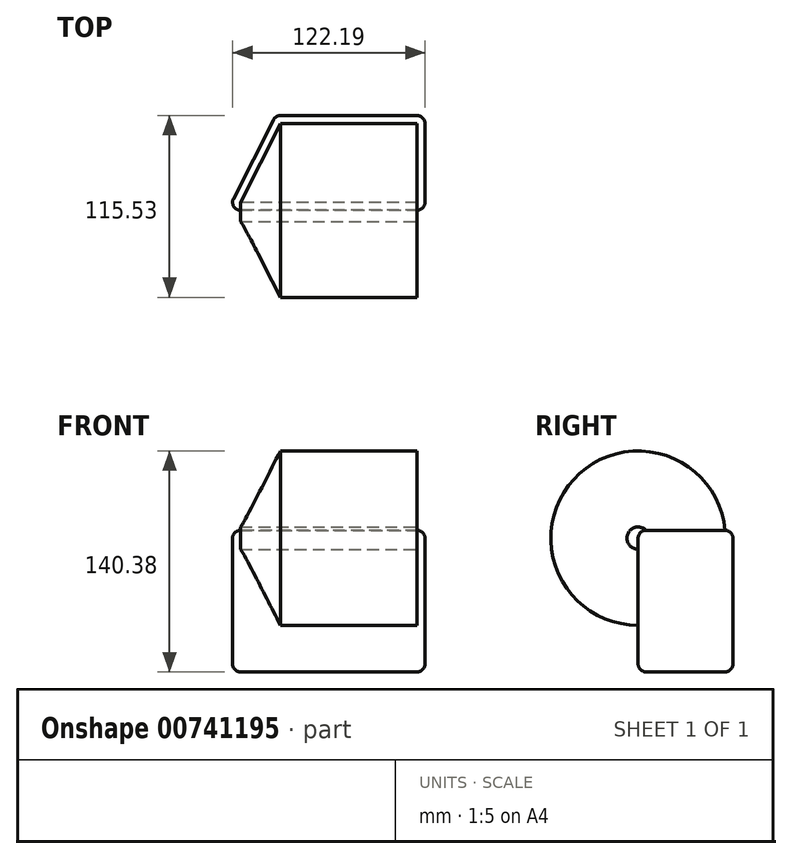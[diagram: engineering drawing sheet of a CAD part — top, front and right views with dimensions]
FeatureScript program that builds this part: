
annotation { "Feature Type Name" : "Feature", "Feature Type Description" : "" }
export const myFeature = defineFeature(function(context is Context, id is Id, definition is map)
    precondition{}
    {
        {
            var Q0;
            Q0=qCreatedBy(makeId("Top.planeOp"),FACE);
            var sketch = newSketch(context, id + "F0", { "sketchPlane" : qUnion([Q0])});
            skLineSegment(sketch, "E0", {"start": v(0, 0) * mm, "end": v(-125.32, 0) * mm});
            skLineSegment(sketch, "E1", {"start": v(-125.32, 0) * mm, "end": v(-94.92, 60.15) * mm});
            skLineSegment(sketch, "E2", {"start": v(-94.92, 60.15) * mm, "end": v(0, 60.15) * mm});
            skLineSegment(sketch, "E3", {"start": v(0, 60.15) * mm, "end": v(0, 0) * mm});
            skSolve(sketch);
        }
        {
            var Q0;
            Q0=makeQuery(id+"F0.imprint","IMPRINT",FACE,{"disambiguationData":[TD([[makeQuery(id+"F0.imprint","IMPRINT",EDGE,{"derivedFrom":sQuery(id+"F0.wireOp",EDGE,"E0")}),-1.0]])]});
            extrude(context, id + "F1", {"entities" : qUnion([Q0]), "depth" : 90 * mm, "offsetDistance" : 25 * mm});
        }
        {
            var Q0;
            Q0=makeQuery(id+"F1.opExtrude","CAP_EDGE",EDGE,{"disambiguationData":[OSD([sQuery(id+"F0.wireOp",EDGE,"E2")])],"isStart":false});
            var Q1;
            Q1=makeQuery(id+"F1.opExtrude","CAP_EDGE",EDGE,{"disambiguationData":[OSD([sQuery(id+"F0.wireOp",EDGE,"E3")])],"isStart":false});
            var Q2;
            Q2=makeQuery(id+"F1.opExtrude","CAP_EDGE",EDGE,{"disambiguationData":[OSD([sQuery(id+"F0.wireOp",EDGE,"E0")])],"isStart":false});
            var Q3;
            Q3=makeQuery(id+"F1.opExtrude","CAP_EDGE",EDGE,{"disambiguationData":[OSD([sQuery(id+"F0.wireOp",EDGE,"E1")])],"isStart":false});
            var Q4;
            Q4=makeQuery(id+"F1.opExtrude","SWEPT_EDGE",EDGE,{"disambiguationData":[OSD([sQuery(id+"F0.wireOp",EDGE,"E2"),sQuery(id+"F0.wireOp",EDGE,"E3")])]});
            var Q5;
            Q5=makeQuery(id+"F1.opExtrude","SWEPT_EDGE",EDGE,{"disambiguationData":[OSD([sQuery(id+"F0.wireOp",EDGE,"E0"),sQuery(id+"F0.wireOp",EDGE,"E3")])]});
            var Q6;
            Q6=makeQuery(id+"F1.opExtrude","SWEPT_EDGE",EDGE,{"disambiguationData":[OSD([sQuery(id+"F0.wireOp",EDGE,"E1"),sQuery(id+"F0.wireOp",EDGE,"E2")])]});
            var Q7;
            Q7=makeQuery(id+"F1.opExtrude","SWEPT_EDGE",EDGE,{"disambiguationData":[OSD([sQuery(id+"F0.wireOp",EDGE,"E0"),sQuery(id+"F0.wireOp",EDGE,"E1")])]});
            var Q8;
            Q8=makeQuery(id+"F1.opExtrude","CAP_EDGE",EDGE,{"disambiguationData":[OSD([sQuery(id+"F0.wireOp",EDGE,"E1")])],"isStart":true});
            var Q9;
            Q9=makeQuery(id+"F1.opExtrude","CAP_EDGE",EDGE,{"disambiguationData":[OSD([sQuery(id+"F0.wireOp",EDGE,"E0")])],"isStart":true});
            var Q10;
            Q10=makeQuery(id+"F1.opExtrude","CAP_EDGE",EDGE,{"disambiguationData":[OSD([sQuery(id+"F0.wireOp",EDGE,"E2")])],"isStart":true});
            var Q11;
            Q11=makeQuery(id+"F1.opExtrude","CAP_EDGE",EDGE,{"disambiguationData":[OSD([sQuery(id+"F0.wireOp",EDGE,"E3")])],"isStart":true});
            fillet(context, id + "F2", {"entities" : qUnion([Q0, Q1, Q2, Q3, Q4, Q5, Q6, Q7, Q8, Q9, Q10, Q11]), "radius" : 5 * mm, "tangentPropagation" : true, "allowEdgeOverflow" : false});
        }
        {
            var Q0;
            Q0=makeQuery(id+"F1.opExtrude","CAP_FACE",FACE,{"disambiguationData":[OSD([sQuery(id+"F0.wireOp",EDGE,"E0"),sQuery(id+"F0.wireOp",EDGE,"E1"),sQuery(id+"F0.wireOp",EDGE,"E2"),sQuery(id+"F0.wireOp",EDGE,"E3")])],"isStart":false});
            var Q1;
            {var subQ0=sQuery(id+"F0.wireOp",EDGE,"E0");Q1=makeQuery(id+"F2.opFillet","BLEND_EDGE",EDGE,{"blendedFrom":[makeQuery(id+"F1.opExtrude","CAP_EDGE",EDGE,{"disambiguationData":[OSD([subQ0])],"isStart":false}),makeQuery(id+"F1.opExtrude","SWEPT_FACE",FACE,{"disambiguationData":[OSD([subQ0])]})],"blendedInto":[makeQuery(id+"F1.opExtrude","SWEPT_FACE",FACE,{"disambiguationData":[OSD([subQ0])]})]});}
            revolve(context, id + "F3", {"operationType" : NewBodyOperationType.ADD, "surfaceOperationType" : NewSurfaceOperationType.NEW, "entities" : qUnion([Q0]), "axis" : qUnion([Q1]), "revolveType" : RevolveType.FULL});
        }
    });
